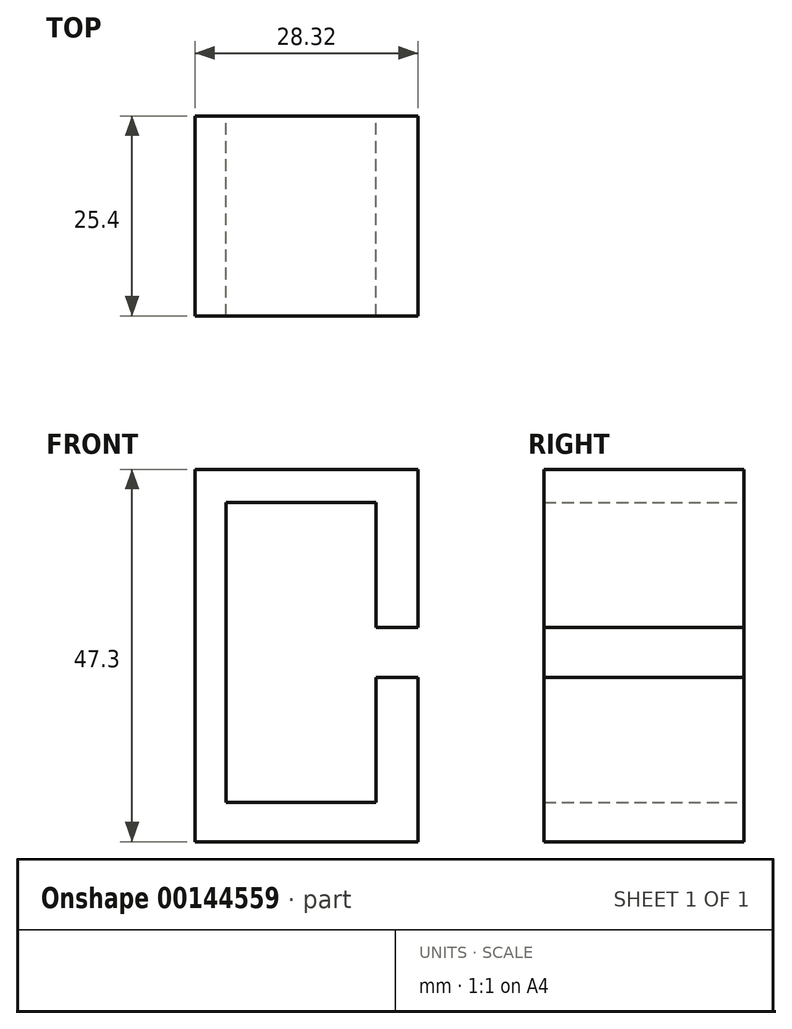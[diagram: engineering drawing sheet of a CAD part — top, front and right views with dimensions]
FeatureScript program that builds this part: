
annotation { "Feature Type Name" : "Feature", "Feature Type Description" : "" }
export const myFeature = defineFeature(function(context is Context, id is Id, definition is map)
    precondition{}
    {
        {
            var Q0;
            Q0=qCreatedBy(makeId("Front.planeOp"),FACE);
            cPlane(context, id + "F0", {"entities" : qUnion([Q0]), "cplaneType" : CPlaneType.OFFSET, "offset" : 25.4 * mm, "width" : 152.4 * mm, "height" : 152.4 * mm});
        }
        {
            var Q0;
            Q0=qCreatedBy(id+"F0.planeOp",FACE);
            var sketch = newSketch(context, id + "F1", { "sketchPlane" : qUnion([Q0])});
            skLineSegment(sketch, "E0.bottom", {"start": v(-12.7, 18.7) * mm, "end": v(6.35, 18.7) * mm});
            skLineSegment(sketch, "E0.top", {"start": v(-12.7, -19.4) * mm, "end": v(6.35, -19.4) * mm});
            skLineSegment(sketch, "E0.left", {"start": v(-12.7, 18.7) * mm, "end": v(-12.7, -19.4) * mm});
            skLineSegment(sketch, "E1", {"start": v(6.35, -3.53) * mm, "end": v(6.35, -19.4) * mm});
            skLineSegment(sketch, "E2", {"start": v(6.35, 2.82) * mm, "end": v(6.35, 18.7) * mm});
            skLineSegment(sketch, "E3", {"start": v(6.35, 2.82) * mm, "end": v(-1.27, 2.82) * mm});
            skLineSegment(sketch, "E4.bottom", {"start": v(-1.27, 2.82) * mm, "end": v(6.35, 2.82) * mm});
            skLineSegment(sketch, "E4.top", {"start": v(-1.27, -3.53) * mm, "end": v(6.35, -3.53) * mm});
            skLineSegment(sketch, "E4.left", {"start": v(-1.27, 2.82) * mm, "end": v(-1.27, -3.53) * mm});
            skLineSegment(sketch, "E5.bottom", {"start": v(-16.64, 22.92) * mm, "end": v(11.68, 22.92) * mm});
            skLineSegment(sketch, "E5.top", {"start": v(-16.64, -24.38) * mm, "end": v(11.68, -24.38) * mm});
            skLineSegment(sketch, "E5.left", {"start": v(-16.64, 22.92) * mm, "end": v(-16.64, -24.38) * mm});
            skLineSegment(sketch, "E5.right", {"start": v(11.68, 22.92) * mm, "end": v(11.68, -24.38) * mm});
            skLineSegment(sketch, "E6", {"start": v(6.35, 2.82) * mm, "end": v(11.68, 2.82) * mm});
            skLineSegment(sketch, "E7", {"start": v(6.35, -3.53) * mm, "end": v(11.68, -3.53) * mm});
            skSolve(sketch);
        }
        {
            var Q0;
            Q0=makeQuery(id+"F1.imprint","IMPRINT",FACE,{"disambiguationData":[TD([[makeQuery(id+"F1.imprint","IMPRINT",EDGE,{"derivedFrom":sQuery(id+"F1.wireOp",EDGE,"E0.bottom")}),1.0]])]});
            extrude(context, id + "F2", {"entities" : qUnion([Q0]), "depth" : 25.4 * mm});
        }
    });
